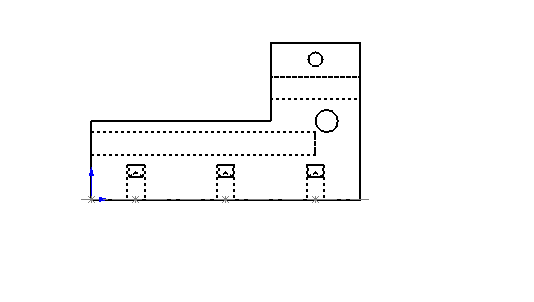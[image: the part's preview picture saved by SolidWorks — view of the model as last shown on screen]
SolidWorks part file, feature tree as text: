
SOLIDWORKS PART (.sldprt)
format: sldprt  version: not decoded by parser v0  size: 317,952 bytes
history: native  units: mm
features: sketch x10, cut_extrude x6, extrude x1, hole x1 (+11 scaffold rows collapsed)
feature tree (29):
  scaffold x11  (default folders/planes/origin — collapsed)
  sketch  "Sketch1"  dims[D1=76.2mm D2=44.45mm]
  extrude  "Extrude1"  Depth=9.525mm
  sketch  "Sketch2"  dims[D1=6.35mm D2=4.7625mm D3=12.7mm]
  cut_extrude  "Cut-Extrude1"  [1 undecoded]
  sketch  "Sketch3"  dims[D1=1.5875mm D2=12.7mm D3=3.9624mm D4=~2.202216mm]
  cut_extrude  "Cut-Extrude2"  [1 undecoded]
  sketch  "Sketch5"  dims[D1=3.9624mm D2=12.7mm D3=4.7625mm]
  cut_extrude  "Cut-Extrude3"  [1 undecoded]
  sketch  "Sketch6"  dims[D1=6.35mm D2=4.7625mm D3=15.875mm]
  cut_extrude  "Cut-Extrude4"  Depth=63.5mm
  sketch  "Sketch7"  dims[D1=12.7mm D2=12.7mm D3=38.1mm]
  hole  "#10-32 Tapped Hole1"  Diameter=4.0386mm Depth=6.441008mm
  sketch  "3DSketch1"
  sketch  "Sketch8"  dims[hole-wizard template sketch: 28 standard entries collapsed; hole parameters kept: c8.Tap Drill Dia.=4.0386mm c8.Tap Drill Depth=~6.441008mm c8.Thread Major Dia.=4.826mm c8.Thread Depth=9.652mm c8.D5=~14.816244mm c8.Drill Angle=118.0deg]
  sketch  "Sketch9"  dims[D3=6.35mm D1=9.525mm D2=22.225mm]
  cut_extrude  "Cut-Extrude5"  Depth=6.35mm
  sketch  "Sketch11"  dims[D1=~6.436243mm D2=~6.612994mm D3=9.525mm D4=25.4mm]
  cut_extrude  "Cut-Extrude6"  [1 undecoded]
decode coverage: 13 of 18 modeling features carry decoded parameters
note: ~ marks probable driven/reference dimensions
note: 4 parameter values undecoded
summary: no parameter record found for 4 features
note: suppression state not decoded; provenance and decode notes live in map.json
